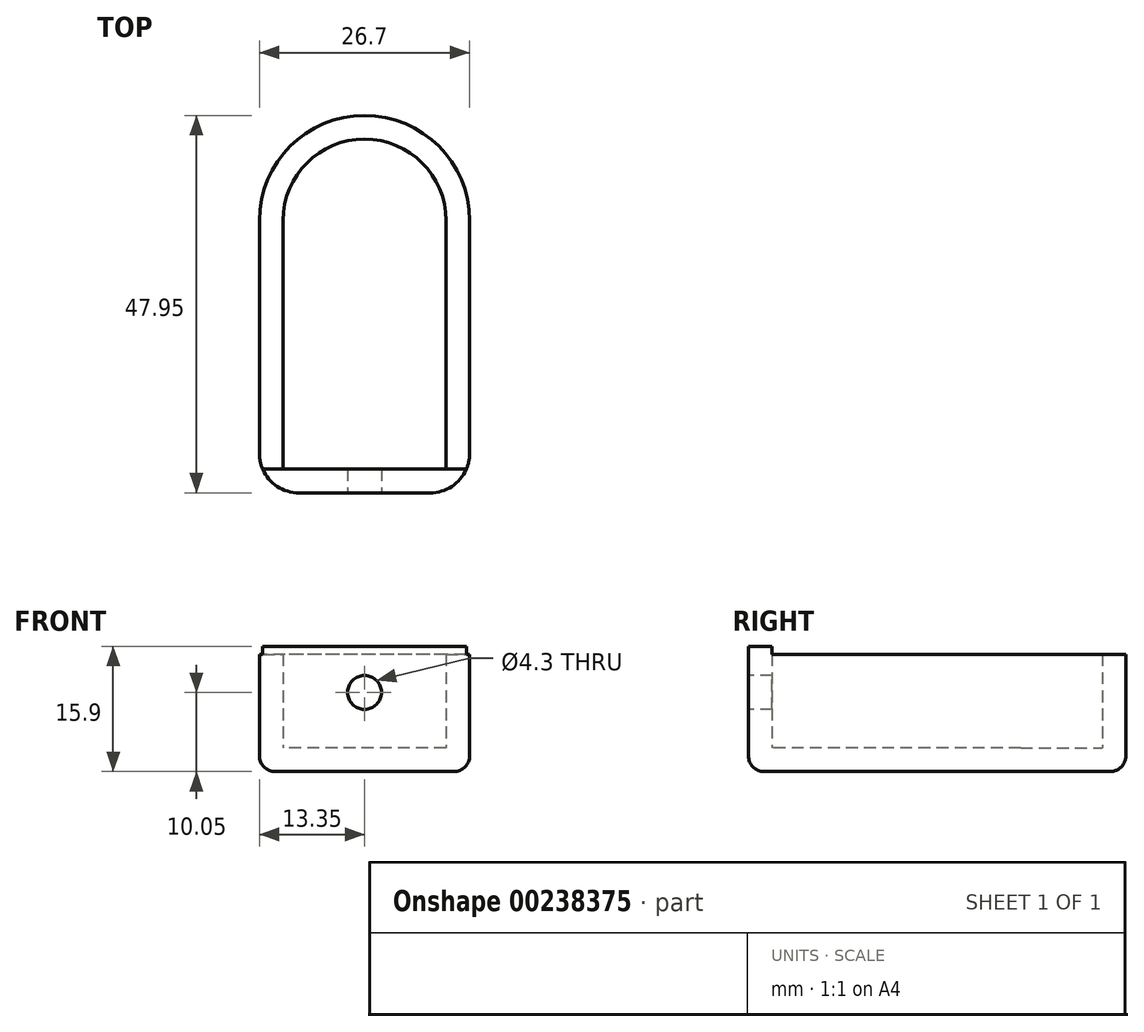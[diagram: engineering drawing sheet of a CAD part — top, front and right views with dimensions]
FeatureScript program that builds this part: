
annotation { "Feature Type Name" : "Feature", "Feature Type Description" : "" }
export const myFeature = defineFeature(function(context is Context, id is Id, definition is map)
    precondition{}
    {
        {
            var Q0;
            Q0=qCreatedBy(makeId("Top.planeOp"),FACE);
            var sketch = newSketch(context, id + "F0", { "sketchPlane" : qUnion([Q0])});
            skArc(sketch, "E0", {"start": v(13.35, 0) * mm, "mid": v(0, 13.35) * mm, "end": v(-13.35, 0) * mm});
            skLineSegment(sketch, "E1", {"start": v(-13.35, 0) * mm, "end": v(-13.35, -34.6) * mm});
            skLineSegment(sketch, "E2", {"start": v(13.35, 0) * mm, "end": v(13.35, -34.6) * mm});
            skLineSegment(sketch, "E3", {"start": v(13.35, -34.6) * mm, "end": v(-13.35, -34.6) * mm});
            skPoint(sketch, "E4.orphan", {"position": v(0, -34.6) * mm});
            skPoint(sketch, "E5.end.orphan", {"position": v(0, 13.35) * mm});
            skLineSegment(sketch, "E6.0", {"start": v(-10.35, 0) * mm, "end": v(-10.35, -31.6) * mm});
            skArc(sketch, "E6.1", {"start": v(10.35, 0) * mm, "mid": v(0, 10.35) * mm, "end": v(-10.35, 0) * mm});
            skLineSegment(sketch, "E6.2", {"start": v(10.35, 0) * mm, "end": v(10.35, -31.6) * mm});
            skLineSegment(sketch, "E6.3", {"start": v(10.35, -31.6) * mm, "end": v(-10.35, -31.6) * mm});
            skSolve(sketch);
        }
        {
            var Q0;
            Q0=makeQuery(id+"F0.imprint","IMPRINT",FACE,{"disambiguationData":[TD([[makeQuery(id+"F0.imprint","IMPRINT",EDGE,{"derivedFrom":sQuery(id+"F0.wireOp",EDGE,"E0")}),1.0]])]});
            var Q1;
            Q1=makeQuery(id+"F0.imprint","IMPRINT",FACE,{"disambiguationData":[TD([[makeQuery(id+"F0.imprint","IMPRINT",EDGE,{"derivedFrom":sQuery(id+"F0.wireOp",EDGE,"E6.0")}),1.0]])]});
            extrude(context, id + "F1", {"entities" : qUnion([Q0, Q1]), "oppositeDirection" : true, "depth" : 3 * mm});
        }
        {
            var Q0;
            Q0=makeQuery(id+"F0.imprint","IMPRINT",FACE,{"disambiguationData":[TD([[makeQuery(id+"F0.imprint","IMPRINT",EDGE,{"derivedFrom":sQuery(id+"F0.wireOp",EDGE,"E0")}),1.0]])]});
            extrude(context, id + "F2", {"entities" : qUnion([Q0]), "operationType" : NewBodyOperationType.ADD, "depth" : 11.9 * mm});
        }
        {
            var Q0;
            Q0=makeQuery(id+"F2.opExtrude","CAP_FACE",FACE,{"disambiguationData":[OSD([sQuery(id+"F0.wireOp",EDGE,"E0"),sQuery(id+"F0.wireOp",EDGE,"E1"),sQuery(id+"F0.wireOp",EDGE,"E2"),sQuery(id+"F0.wireOp",EDGE,"E3"),sQuery(id+"F0.wireOp",EDGE,"E6.0"),sQuery(id+"F0.wireOp",EDGE,"E6.1"),sQuery(id+"F0.wireOp",EDGE,"E6.2"),sQuery(id+"F0.wireOp",EDGE,"E6.3")])],"isStart":false});
            var sketch = newSketch(context, id + "F3", { "sketchPlane" : qUnion([Q0])});
            skLineSegment(sketch, "E7.0", {"start": v(13.35, -34.6) * mm, "end": v(-13.35, -34.6) * mm});
            skLineSegment(sketch, "E8", {"start": v(-13.35, -34.6) * mm, "end": v(-13.35, -31.6) * mm});
            skLineSegment(sketch, "E9", {"start": v(-13.35, -31.6) * mm, "end": v(13.35, -31.6) * mm});
            skLineSegment(sketch, "E10", {"start": v(13.35, -31.6) * mm, "end": v(13.35, -34.6) * mm});
            skSolve(sketch);
        }
        {
            var Q0;
            Q0=makeQuery(id+"F3.imprint","IMPRINT",FACE,{"disambiguationData":[TD([[makeQuery(id+"F3.imprint","IMPRINT",EDGE,{"derivedFrom":sQuery(id+"F3.wireOp",EDGE,"E7.0")}),-1.0]])]});
            extrude(context, id + "F4", {"entities" : qUnion([Q0]), "operationType" : NewBodyOperationType.ADD, "depth" : 1 * mm});
        }
        {
            var Q0;
            {var subQ0=sQuery(id+"F0.wireOp",EDGE,"E3");Q0=makeQuery(id+"F4.boolean.opBoolean","MERGE",FACE,{"derivedFrom":[makeQuery(id+"F2.boolean.opBoolean","MERGE",FACE,{"derivedFrom":[makeQuery(id+"F1.opExtrude","SWEPT_FACE",FACE,{"disambiguationData":[OSD([subQ0])]}),makeQuery(id+"F2.opExtrude","SWEPT_FACE",FACE,{"disambiguationData":[OSD([subQ0])]})]}),makeQuery(id+"F4.opExtrude","SWEPT_FACE",FACE,{"disambiguationData":[OSD([sQuery(id+"F3.wireOp",EDGE,"E7.0")])]})]});}
            var sketch = newSketch(context, id + "F5", { "sketchPlane" : qUnion([Q0])});
            skLineSegment(sketch, "E11.0", {"start": v(13.35, -3) * mm, "end": v(-13.35, -3) * mm});
            skLineSegment(sketch, "E12", {"start": v(-13.35, 4.9) * mm, "end": v(13.35, 4.9) * mm});
            skLineSegment(sketch, "E13", {"start": v(-13.35, 9.2) * mm, "end": v(13.35, 9.2) * mm});
            skLineSegment(sketch, "E14", {"start": v(0, 9.2) * mm, "end": v(0, 4.9) * mm});
            skCircle(sketch, "E15", {"center": v(0, 7.05) * mm, "radius": 2.15 * mm});
            skSolve(sketch);
        }
        {
            var Q0;
            {var subQ0=sQuery(id+"F5.wireOp",EDGE,"E14");Q0=makeQuery(id+"F5.imprint","IMPRINT",FACE,{"disambiguationData":[TD([[makeQuery(id+"F5.imprint","IMPRINT",EDGE,{"derivedFrom":subQ0}),-1.0]])]});}
            var Q1;
            {var subQ0=sQuery(id+"F5.wireOp",EDGE,"E14");Q1=makeQuery(id+"F5.imprint","IMPRINT",FACE,{"disambiguationData":[TD([[makeQuery(id+"F5.imprint","IMPRINT",EDGE,{"derivedFrom":subQ0}),1.0]])]});}
            extrude(context, id + "F6", {"entities" : qUnion([Q0, Q1]), "operationType" : NewBodyOperationType.REMOVE, "oppositeDirection" : true, "depth" : 6 * mm});
        }
        {
            var Q0;
            {var subQ0=sQuery(id+"F0.wireOp",EDGE,"E3");var subQ1=sQuery(id+"F0.wireOp",EDGE,"E1");Q0=makeQuery(id+"F4.boolean.opBoolean","MERGE",EDGE,{"derivedFrom":[makeQuery(id+"F2.boolean.opBoolean","MERGE",EDGE,{"derivedFrom":[makeQuery(id+"F1.opExtrude","SWEPT_EDGE",EDGE,{"disambiguationData":[OSD([subQ1,subQ0])]}),makeQuery(id+"F2.opExtrude","SWEPT_EDGE",EDGE,{"disambiguationData":[OSD([subQ1,subQ0])]})]}),makeQuery(id+"F4.opExtrude","SWEPT_EDGE",EDGE,{"disambiguationData":[OSD([sQuery(id+"F3.wireOp",EDGE,"E7.0"),sQuery(id+"F3.wireOp",EDGE,"E8")])]})]});}
            var Q1;
            {var subQ0=sQuery(id+"F0.wireOp",EDGE,"E3");var subQ1=sQuery(id+"F0.wireOp",EDGE,"E2");Q1=makeQuery(id+"F4.boolean.opBoolean","MERGE",EDGE,{"derivedFrom":[makeQuery(id+"F2.boolean.opBoolean","MERGE",EDGE,{"derivedFrom":[makeQuery(id+"F1.opExtrude","SWEPT_EDGE",EDGE,{"disambiguationData":[OSD([subQ1,subQ0])]}),makeQuery(id+"F2.opExtrude","SWEPT_EDGE",EDGE,{"disambiguationData":[OSD([subQ1,subQ0])]})]}),makeQuery(id+"F4.opExtrude","SWEPT_EDGE",EDGE,{"disambiguationData":[OSD([sQuery(id+"F3.wireOp",EDGE,"E7.0"),sQuery(id+"F3.wireOp",EDGE,"E10")])]})]});}
            fillet(context, id + "F7", {"entities" : qUnion([Q0, Q1]), "radius" : 5 * mm, "tangentPropagation" : true, "allowEdgeOverflow" : false});
        }
        {
            var Q0;
            Q0=makeQuery(id+"F1.opExtrude","CAP_EDGE",EDGE,{"disambiguationData":[OSD([sQuery(id+"F0.wireOp",EDGE,"E2")])],"isStart":false});
            fillet(context, id + "F8", {"entities" : qUnion([Q0]), "radius" : 2 * mm, "tangentPropagation" : true, "allowEdgeOverflow" : false});
        }
        {
            var Q0;
            Q0=makeQuery(id+"F4.boolean.opBoolean","MERGE",FACE,{"derivedFrom":[makeQuery(id+"F2.opExtrude","SWEPT_FACE",FACE,{"disambiguationData":[OSD([sQuery(id+"F0.wireOp",EDGE,"E6.3")])]}),makeQuery(id+"F4.opExtrude","SWEPT_FACE",FACE,{"disambiguationData":[OSD([sQuery(id+"F3.wireOp",EDGE,"E9")])]})]});
            var sketch = newSketch(context, id + "F9", { "sketchPlane" : qUnion([Q0])});
            skCircle(sketch, "E16", {"center": v(0, 7.05) * mm, "radius": 3.53 * mm});
            skSolve(sketch);
        }
        {
            var Q0;
            Q0=qSketchRegion(id+"F9",true);
            extrude(context, id + "F10", {"entities" : qUnion([Q0]), "operationType" : NewBodyOperationType.ADD, "oppositeDirection" : true, "depth" : 1 * mm});
        }
        {
            var Q0;
            Q0=makeQuery(id+"F10.opExtrude","CAP_FACE",FACE,{"disambiguationData":[OSD([sQuery(id+"F9.wireOp",EDGE,"E16")])],"isStart":false});
            extrude(context, id + "F11", {"entities" : qUnion([Q0]), "operationType" : NewBodyOperationType.REMOVE, "oppositeDirection" : true, "depth" : 25 * mm});
        }
    });
